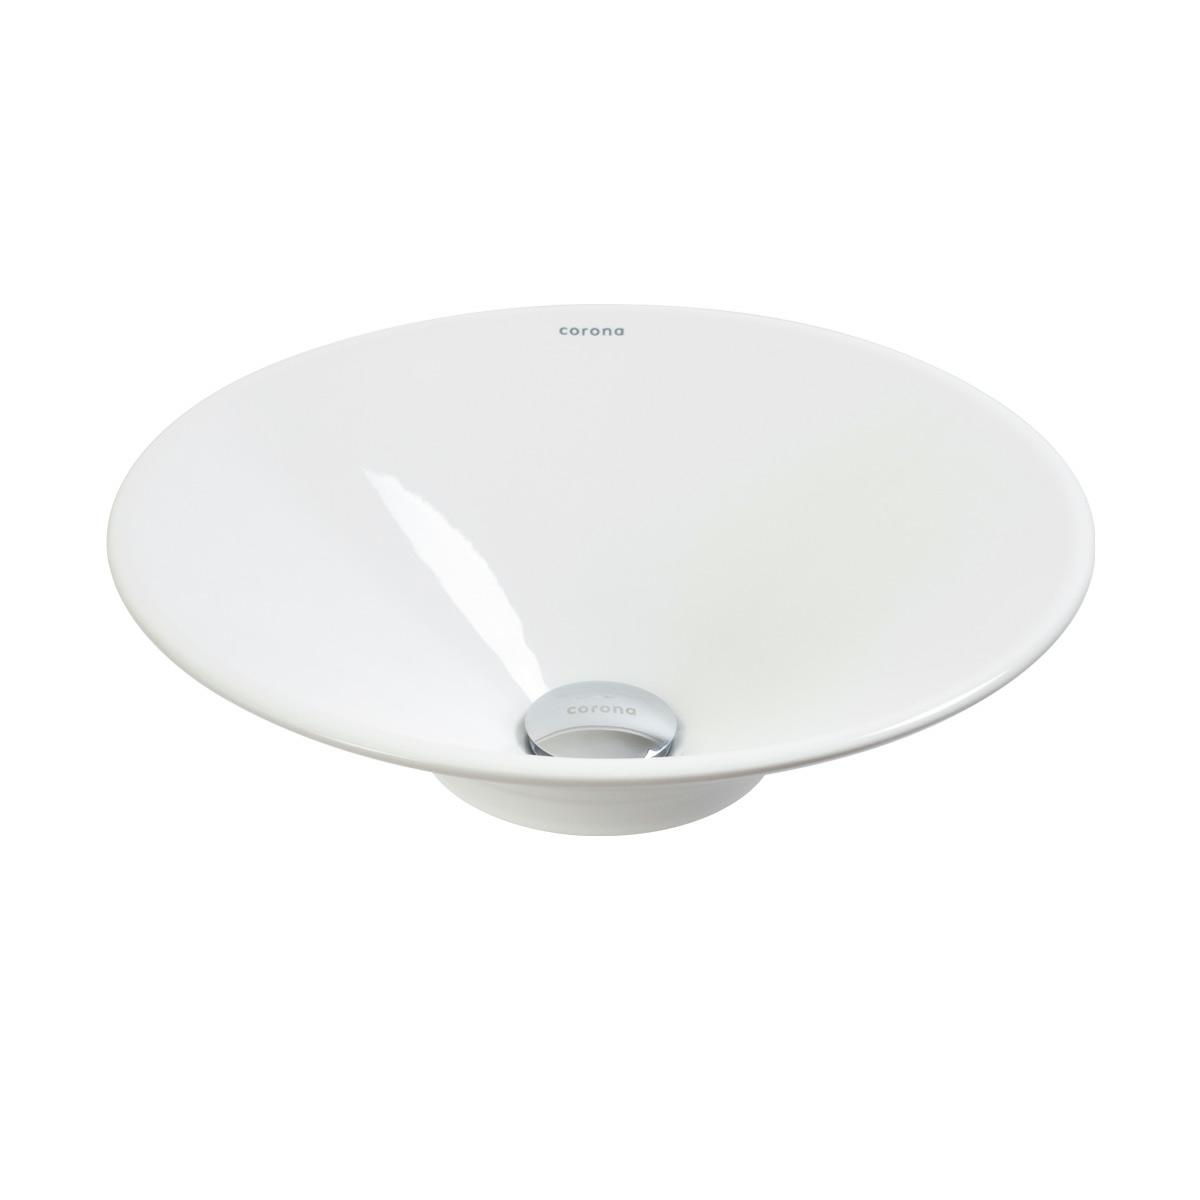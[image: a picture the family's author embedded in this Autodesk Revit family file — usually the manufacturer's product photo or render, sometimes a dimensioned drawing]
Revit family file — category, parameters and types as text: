
# Revit family: CCMX-CORONA_VENTO
name_source: partatom
category: Plumbing Fixtures
units: mm (PartAtom-declared; Revit-internal decimal feet)

## family parameters
Always vertical = Yes
Cut with Voids When Loaded = No
OmniClass Number = 23.45.00.00
OmniClass Title = Sanitary, Laundry, and Cleaning Equipment
Part Type = Normal
Room Calculation Point = No
Round Connector Dimension = Use Diameter
Shared = No
Work Plane-Based = No

## types (1)
- CCMX-CORONA_VENTO
    Assembly Code = D2010.60
    Description = Diseñado para espacios innovadores con líneas simples y modernas. Bowl redondo, cónico con pozo de gran amplitud y comodidad.
    Dimensiones = https://coronamexico.com
    Ficha Tecnica = https://coronamexico.com
    Garantia de Producto = 20 años en porcelana sanitaria
    Keynote = 224116
    Manufacturer = CORONA
    Model = Vento
    Type Image = VENTO.jpg
    URL = https://coronamexico.com

## geometry (parser evidence)
native form markers: Sweep x3
no freeform markers — native parametric forms only
